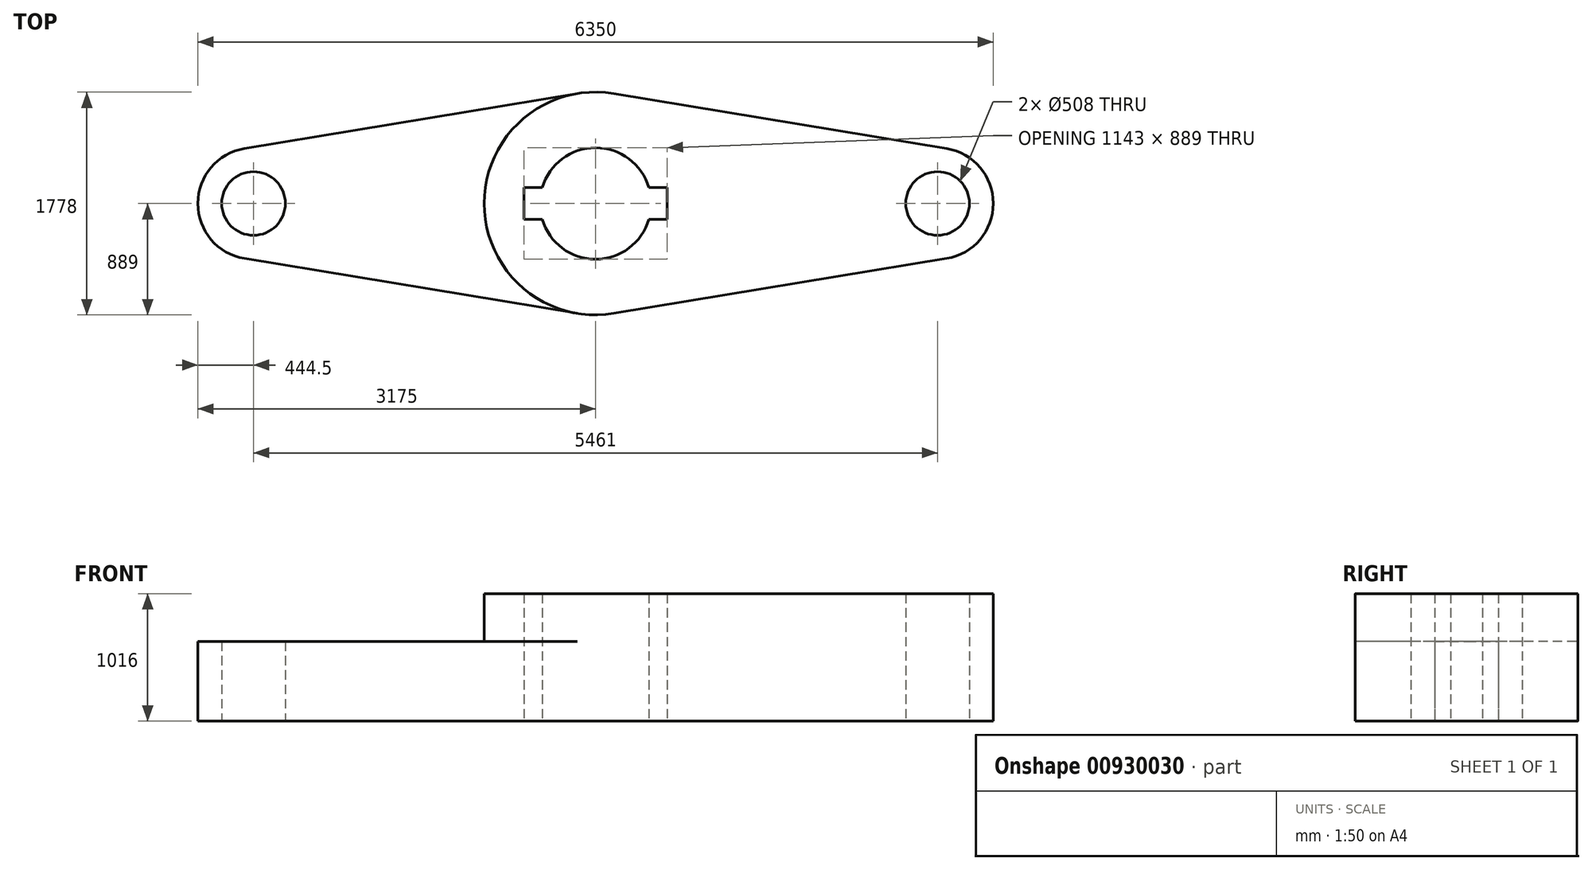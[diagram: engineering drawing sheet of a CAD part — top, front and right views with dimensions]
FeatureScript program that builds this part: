
annotation { "Feature Type Name" : "Feature", "Feature Type Description" : "" }
export const myFeature = defineFeature(function(context is Context, id is Id, definition is map)
    precondition{}
    {
        {
            var Q0;
            Q0=qCreatedBy(makeId("Top.planeOp"),FACE);
            var sketch = newSketch(context, id + "F0", { "sketchPlane" : qUnion([Q0])});
            skCircle(sketch, "E0", {"center": v(0, 0) * mm, "radius": 889 * mm});
            skCircle(sketch, "E1", {"center": v(0, 0) * mm, "radius": 444.5 * mm});
            skCircle(sketch, "E2", {"center": v(2730.5, 0) * mm, "radius": 254 * mm});
            skCircle(sketch, "E3", {"center": v(2730.5, 0) * mm, "radius": 444.5 * mm});
            skCircle(sketch, "E4", {"center": v(-2730.5, 0) * mm, "radius": 444.5 * mm});
            skCircle(sketch, "E5", {"center": v(-2730.5, 0) * mm, "radius": 254 * mm});
            skLineSegment(sketch, "E6", {"start": v(0, 0) * mm, "end": v(0, 54.95) * mm, "construction": true});
            skLineSegment(sketch, "E7.bottom", {"start": v(571.5, 127) * mm, "end": v(-571.5, 127) * mm});
            skLineSegment(sketch, "E7.top", {"start": v(571.5, -127) * mm, "end": v(-571.5, -127) * mm});
            skLineSegment(sketch, "E7.left", {"start": v(571.5, 127) * mm, "end": v(571.5, -127) * mm});
            skLineSegment(sketch, "E7.right", {"start": v(-571.5, 127) * mm, "end": v(-571.5, -127) * mm});
            skLineSegment(sketch, "E8", {"start": v(-144.72, 877.14) * mm, "end": v(-2802.86, 438.57) * mm});
            skLineSegment(sketch, "E9", {"start": v(-2802.86, -438.57) * mm, "end": v(-144.72, -877.14) * mm});
            skLineSegment(sketch, "E10", {"start": v(144.72, -877.14) * mm, "end": v(2802.86, -438.57) * mm});
            skLineSegment(sketch, "E11", {"start": v(144.72, 877.14) * mm, "end": v(2802.86, 438.57) * mm});
            skSolve(sketch);
        }
        {
            var Q0;
            {var subQ6=sQuery(id+"F0.wireOp",EDGE,"E7.left");Q0=makeQuery(id+"F0.imprint","IMPRINT",FACE,{"disambiguationData":[TD([[makeQuery(id+"F0.imprint","IMPRINT",EDGE,{"derivedFrom":subQ6}),1.0]])]});}
            var Q1;
            {var subQ0=sQuery(id+"F0.wireOp",EDGE,"E10");Q1=makeQuery(id+"F0.imprint","IMPRINT",FACE,{"disambiguationData":[TD([[makeQuery(id+"F0.imprint","IMPRINT",EDGE,{"derivedFrom":subQ0}),1.0]])]});}
            var Q2;
            Q2=makeQuery(id+"F0.imprint","IMPRINT",FACE,{"disambiguationData":[TD([[makeQuery(id+"F0.imprint","IMPRINT",EDGE,{"derivedFrom":sQuery(id+"F0.wireOp",EDGE,"E2")}),-1.0]])]});
            extrude(context, id + "F1", {"entities" : qUnion([Q0, Q1, Q2]), "depth" : 1016 * mm, "offsetDistance" : 25.4 * mm});
        }
        {
            var Q0;
            Q0 = qSketchRegion(id + "F0", true);
            extrude(context, id + "F2", {"entities" : qUnion([Q0]), "operationType" : NewBodyOperationType.ADD, "depth" : 635 * mm, "offsetDistance" : 25.4 * mm});
        }
    });
